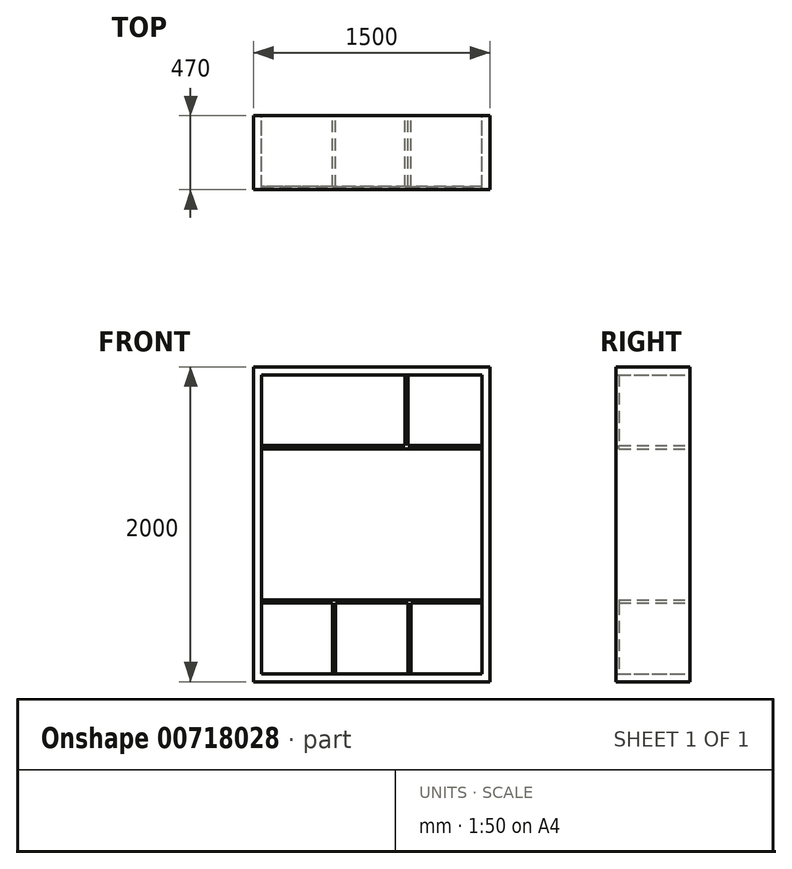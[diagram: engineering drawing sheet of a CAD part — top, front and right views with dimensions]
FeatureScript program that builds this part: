
annotation { "Feature Type Name" : "Feature", "Feature Type Description" : "" }
export const myFeature = defineFeature(function(context is Context, id is Id, definition is map)
    precondition{}
    {
        {
            var Q0;
            Q0=qCreatedBy(makeId("Front.planeOp"),FACE);
            var sketch = newSketch(context, id + "F0", { "sketchPlane" : qUnion([Q0])});
            skLineSegment(sketch, "E0.bottom", {"start": v(750, 1000) * mm, "end": v(-750, 1000) * mm});
            skLineSegment(sketch, "E0.top", {"start": v(750, -1000) * mm, "end": v(-750, -1000) * mm});
            skLineSegment(sketch, "E0.left", {"start": v(750, 1000) * mm, "end": v(750, -1000) * mm});
            skLineSegment(sketch, "E0.right", {"start": v(-750, 1000) * mm, "end": v(-750, -1000) * mm});
            skPoint(sketch, "E0.middle", {"position": v(0, 0) * mm});
            skLineSegment(sketch, "E1.0", {"start": v(700, 950) * mm, "end": v(-700, 950) * mm});
            skLineSegment(sketch, "E1.1", {"start": v(700, 950) * mm, "end": v(700, -950) * mm});
            skLineSegment(sketch, "E1.2", {"start": v(700, -950) * mm, "end": v(-700, -950) * mm});
            skLineSegment(sketch, "E1.3", {"start": v(-700, 950) * mm, "end": v(-700, -950) * mm});
            skSolve(sketch);
        }
        {
            var Q0;
            Q0 = qSketchRegion(id + "F0", true);
            extrude(context, id + "F1", {"entities" : qUnion([Q0]), "depth" : 470 * mm, "offsetDistance" : 25 * mm});
        }
        {
            var Q0;
            Q0=qCreatedBy(makeId("Front.planeOp"),FACE);
            var sketch = newSketch(context, id + "F2", { "sketchPlane" : qUnion([Q0])});
            skLineSegment(sketch, "E2.bottom", {"start": v(700, -480) * mm, "end": v(-700, -480) * mm});
            skLineSegment(sketch, "E2.top", {"start": v(700, -500) * mm, "end": v(-700, -500) * mm});
            skLineSegment(sketch, "E2.left", {"start": v(700, -480) * mm, "end": v(700, -500) * mm});
            skLineSegment(sketch, "E2.right", {"start": v(-700, -480) * mm, "end": v(-700, -500) * mm});
            skPoint(sketch, "E2.middle", {"position": v(0, -490) * mm});
            skLineSegment(sketch, "E3.bottom", {"start": v(-250, -500) * mm, "end": v(-230, -500) * mm});
            skLineSegment(sketch, "E3.top", {"start": v(-250, -950) * mm, "end": v(-230, -950) * mm});
            skLineSegment(sketch, "E3.left", {"start": v(-250, -500) * mm, "end": v(-250, -950) * mm});
            skLineSegment(sketch, "E3.right", {"start": v(-230, -500) * mm, "end": v(-230, -950) * mm});
            skLineSegment(sketch, "E4.bottom", {"start": v(230, -500) * mm, "end": v(250, -500) * mm});
            skLineSegment(sketch, "E4.top", {"start": v(230, -950) * mm, "end": v(250, -950) * mm});
            skLineSegment(sketch, "E4.left", {"start": v(230, -500) * mm, "end": v(230, -950) * mm});
            skLineSegment(sketch, "E4.right", {"start": v(250, -500) * mm, "end": v(250, -950) * mm});
            skSolve(sketch);
        }
        {
            var Q0;
            Q0 = qSketchRegion(id + "F2", true);
            extrude(context, id + "F3", {"entities" : qUnion([Q0]), "operationType" : NewBodyOperationType.ADD, "depth" : 450 * mm, "offsetDistance" : 25 * mm});
        }
        {
            var Q0;
            Q0=qCreatedBy(makeId("Front.planeOp"),FACE);
            var sketch = newSketch(context, id + "F4", { "sketchPlane" : qUnion([Q0])});
            skLineSegment(sketch, "E5.bottom", {"start": v(-700, 950) * mm, "end": v(230, 950) * mm});
            skLineSegment(sketch, "E5.top", {"start": v(-700, 480) * mm, "end": v(230, 480) * mm});
            skLineSegment(sketch, "E5.left", {"start": v(-700, 950) * mm, "end": v(-700, 480) * mm});
            skLineSegment(sketch, "E5.right", {"start": v(230, 950) * mm, "end": v(230, 480) * mm});
            skLineSegment(sketch, "E6.0", {"start": v(-700, 500) * mm, "end": v(210, 500) * mm});
            skLineSegment(sketch, "E6.1", {"start": v(210, 950) * mm, "end": v(210, 500) * mm});
            skSolve(sketch);
        }
        {
            var Q0;
            {var subQ2=sQuery(id+"F4.wireOp",EDGE,"E5.top");Q0=makeQuery(id+"F4.imprint","IMPRINT",FACE,{"disambiguationData":[TD([[makeQuery(id+"F4.imprint","IMPRINT",EDGE,{"derivedFrom":subQ2}),1.0]])]});}
            extrude(context, id + "F5", {"entities" : qUnion([Q0]), "operationType" : NewBodyOperationType.ADD, "depth" : 450 * mm, "offsetDistance" : 25 * mm});
        }
        {
            var Q0;
            Q0=qCreatedBy(makeId("Front.planeOp"),FACE);
            var sketch = newSketch(context, id + "F6", { "sketchPlane" : qUnion([Q0])});
            skLineSegment(sketch, "E7.bottom", {"start": v(230, 480) * mm, "end": v(700, 480) * mm});
            skLineSegment(sketch, "E7.top", {"start": v(230, 500) * mm, "end": v(700, 500) * mm});
            skLineSegment(sketch, "E7.left", {"start": v(230, 480) * mm, "end": v(230, 500) * mm});
            skLineSegment(sketch, "E7.right", {"start": v(700, 480) * mm, "end": v(700, 500) * mm});
            skSolve(sketch);
        }
        {
            var Q0;
            Q0 = qSketchRegion(id + "F6", true);
            extrude(context, id + "F7", {"entities" : qUnion([Q0]), "operationType" : NewBodyOperationType.ADD, "depth" : 450 * mm, "offsetDistance" : 25 * mm});
        }
    });
